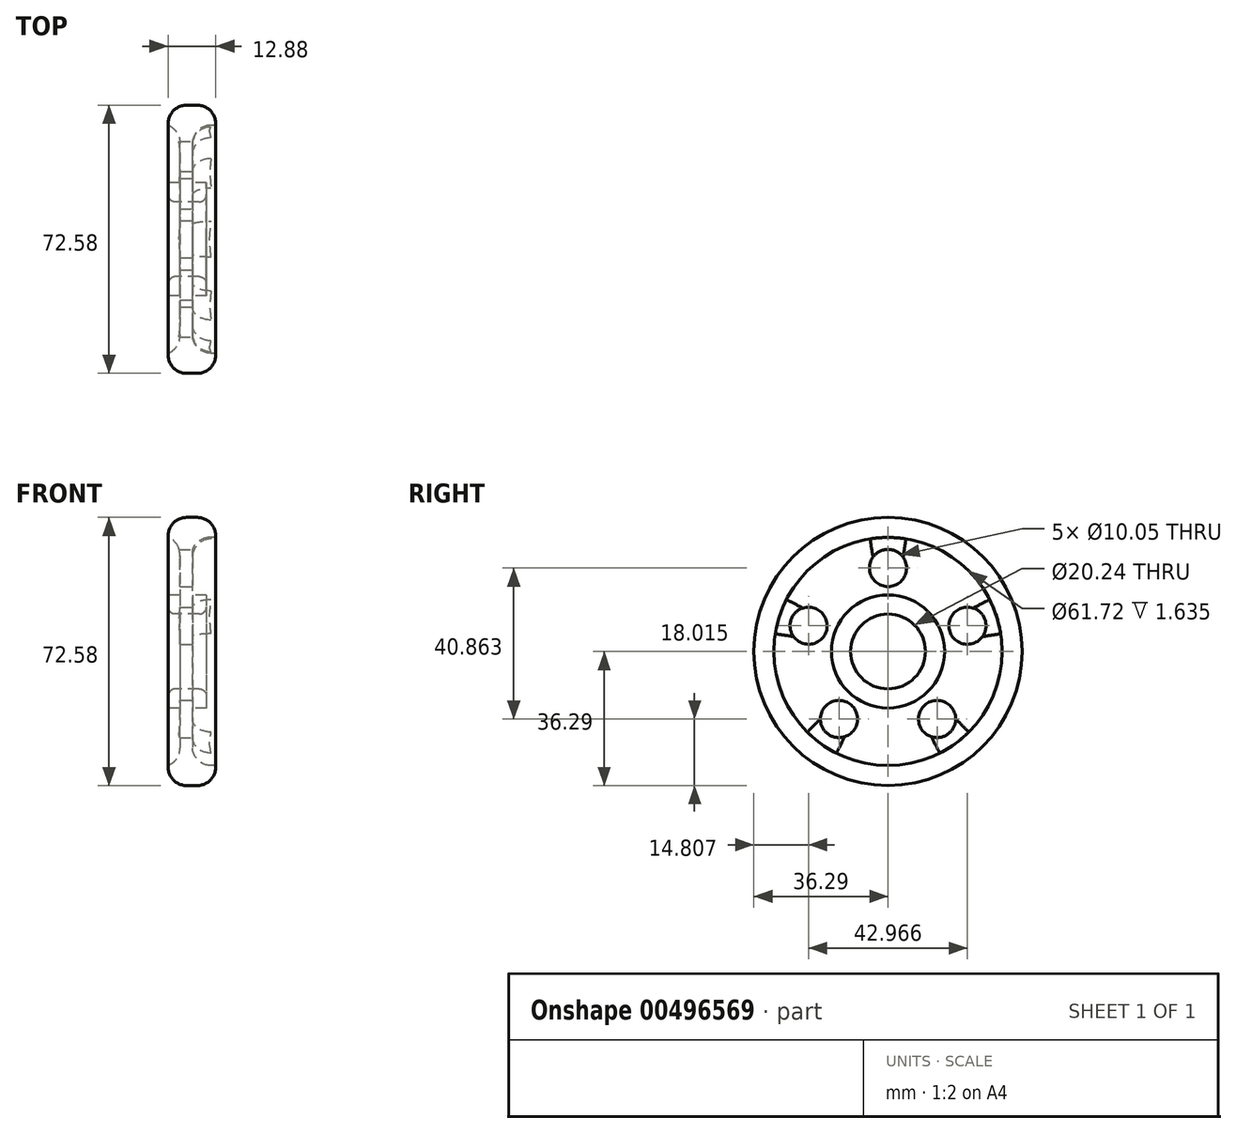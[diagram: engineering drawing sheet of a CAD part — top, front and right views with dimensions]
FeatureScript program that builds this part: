
annotation { "Feature Type Name" : "Feature", "Feature Type Description" : "" }
export const myFeature = defineFeature(function(context is Context, id is Id, definition is map)
    precondition{}
    {
        {
            var Q0;
            Q0=qCreatedBy(makeId("Front.planeOp"),FACE);
            var sketch = newSketch(context, id + "F0", { "sketchPlane" : qUnion([Q0])});
            skLineSegment(sketch, "E0", {"start": v(0, 10.12) * mm, "end": v(10.37, 10.12) * mm});
            skLineSegment(sketch, "E1", {"start": v(10.37, 10.12) * mm, "end": v(10.37, 15.3) * mm});
            skLineSegment(sketch, "E2", {"start": v(10.37, 15.3) * mm, "end": v(6.57, 15.3) * mm});
            skLineSegment(sketch, "E3", {"start": v(6.57, 15.3) * mm, "end": v(6.57, 30.86) * mm});
            skLineSegment(sketch, "E4", {"start": v(6.57, 30.86) * mm, "end": v(12.88, 30.86) * mm});
            skLineSegment(sketch, "E5", {"start": v(12.88, 30.86) * mm, "end": v(12.88, 36.29) * mm});
            skLineSegment(sketch, "E6", {"start": v(12.88, 36.29) * mm, "end": v(0, 36.29) * mm});
            skLineSegment(sketch, "E7", {"start": v(0, 36.29) * mm, "end": v(0, 30.86) * mm});
            skLineSegment(sketch, "E8", {"start": v(0, 30.86) * mm, "end": v(3.2, 30.86) * mm});
            skLineSegment(sketch, "E9", {"start": v(3.2, 30.86) * mm, "end": v(3.2, 15.3) * mm});
            skLineSegment(sketch, "E10", {"start": v(3.2, 15.3) * mm, "end": v(0, 15.3) * mm});
            skLineSegment(sketch, "E11", {"start": v(0, 15.3) * mm, "end": v(0, 10.12) * mm});
            skLineSegment(sketch, "E12", {"start": v(0, 0) * mm, "end": v(10.79, 0) * mm});
            skSolve(sketch);
        }
        {
            var Q0;
            Q0 = qSketchRegion(id + "F0", true);
            var Q1;
            Q1=sQuery(id+"F0.wireOp",EDGE,"E12");
            revolve(context, id + "F1", {"entities" : qUnion([Q0]), "axis" : qUnion([Q1]), "revolveType" : RevolveType.FULL});
        }
        {
            var Q0;
            Q0=makeQuery(id+"F1.opRevolve","SWEPT_FACE",FACE,{"disambiguationData":[OSD([sQuery(id+"F0.wireOp",EDGE,"E1")])]});
            var sketch = newSketch(context, id + "F2", { "sketchPlane" : qUnion([Q0])});
            skCircle(sketch, "E13", {"center": v(0, 22.59) * mm, "radius": 5.03 * mm});
            skCircle(sketch, "E14.1.0", {"center": v(-21.48, 6.98) * mm, "radius": 5.03 * mm});
            skCircle(sketch, "E14.2.0", {"center": v(-13.28, -18.27) * mm, "radius": 5.03 * mm});
            skCircle(sketch, "E14.3.0", {"center": v(13.28, -18.27) * mm, "radius": 5.03 * mm});
            skCircle(sketch, "E14.4.0", {"center": v(21.48, 6.98) * mm, "radius": 5.03 * mm});
            skPoint(sketch, "E14.center", {"position": v(0, 0) * mm});
            skSolve(sketch);
        }
        {
            var Q0;
            Q0=makeQuery(id+"F2.imprint","IMPRINT",FACE,{"disambiguationData":[TD([[makeQuery(id+"F2.imprint","IMPRINT",EDGE,{"derivedFrom":sQuery(id+"F2.wireOp",EDGE,"E14.1.0")}),1.0]])]});
            var Q1;
            Q1=makeQuery(id+"F2.imprint","IMPRINT",FACE,{"disambiguationData":[TD([[makeQuery(id+"F2.imprint","IMPRINT",EDGE,{"derivedFrom":sQuery(id+"F2.wireOp",EDGE,"E14.2.0")}),1.0]])]});
            var Q2;
            Q2=makeQuery(id+"F2.imprint","IMPRINT",FACE,{"disambiguationData":[TD([[makeQuery(id+"F2.imprint","IMPRINT",EDGE,{"derivedFrom":sQuery(id+"F2.wireOp",EDGE,"E14.3.0")}),1.0]])]});
            var Q3;
            Q3=makeQuery(id+"F2.imprint","IMPRINT",FACE,{"disambiguationData":[TD([[makeQuery(id+"F2.imprint","IMPRINT",EDGE,{"derivedFrom":sQuery(id+"F2.wireOp",EDGE,"E14.4.0")}),1.0]])]});
            var Q4;
            Q4=makeQuery(id+"F2.imprint","IMPRINT",FACE,{"disambiguationData":[TD([[makeQuery(id+"F2.imprint","IMPRINT",EDGE,{"derivedFrom":sQuery(id+"F2.wireOp",EDGE,"E13")}),1.0]])]});
            extrude(context, id + "F3", {"entities" : qUnion([Q0, Q1, Q2, Q3, Q4]), "operationType" : NewBodyOperationType.REMOVE, "oppositeDirection" : true, "depth" : 25 * mm});
        }
        {
            var Q0;
            Q0=makeQuery(id+"F1.opRevolve","SWEPT_EDGE",EDGE,{"disambiguationData":[OSD([sQuery(id+"F0.wireOp",EDGE,"E8"),sQuery(id+"F0.wireOp",EDGE,"E9")])]});
            var Q1;
            Q1=makeQuery(id+"F1.opRevolve","SWEPT_EDGE",EDGE,{"disambiguationData":[OSD([sQuery(id+"F0.wireOp",EDGE,"E3"),sQuery(id+"F0.wireOp",EDGE,"E4")])]});
            var Q2;
            Q2=makeQuery(id+"F1.opRevolve","SWEPT_EDGE",EDGE,{"disambiguationData":[OSD([sQuery(id+"F0.wireOp",EDGE,"E6"),sQuery(id+"F0.wireOp",EDGE,"E7")])]});
            var Q3;
            Q3=makeQuery(id+"F1.opRevolve","SWEPT_EDGE",EDGE,{"disambiguationData":[OSD([sQuery(id+"F0.wireOp",EDGE,"E5"),sQuery(id+"F0.wireOp",EDGE,"E6")])]});
            fillet(context, id + "F4", {"entities" : qUnion([Q0, Q1, Q2, Q3]), "radius" : 5 * mm, "tangentPropagation" : true, "allowEdgeOverflow" : false});
        }
        {
            var Q0;
            Q0=makeQuery(id+"F1.opRevolve","SWEPT_EDGE",EDGE,{"disambiguationData":[OSD([sQuery(id+"F0.wireOp",EDGE,"E0"),sQuery(id+"F0.wireOp",EDGE,"E1")])]});
            var Q1;
            Q1=makeQuery(id+"F1.opRevolve","SWEPT_EDGE",EDGE,{"disambiguationData":[OSD([sQuery(id+"F0.wireOp",EDGE,"E0"),sQuery(id+"F0.wireOp",EDGE,"E11")])]});
            fillet(context, id + "F5", {"entities" : qUnion([Q0, Q1]), "radius" : 2 * mm, "tangentPropagation" : true, "allowEdgeOverflow" : false});
        }
    });
